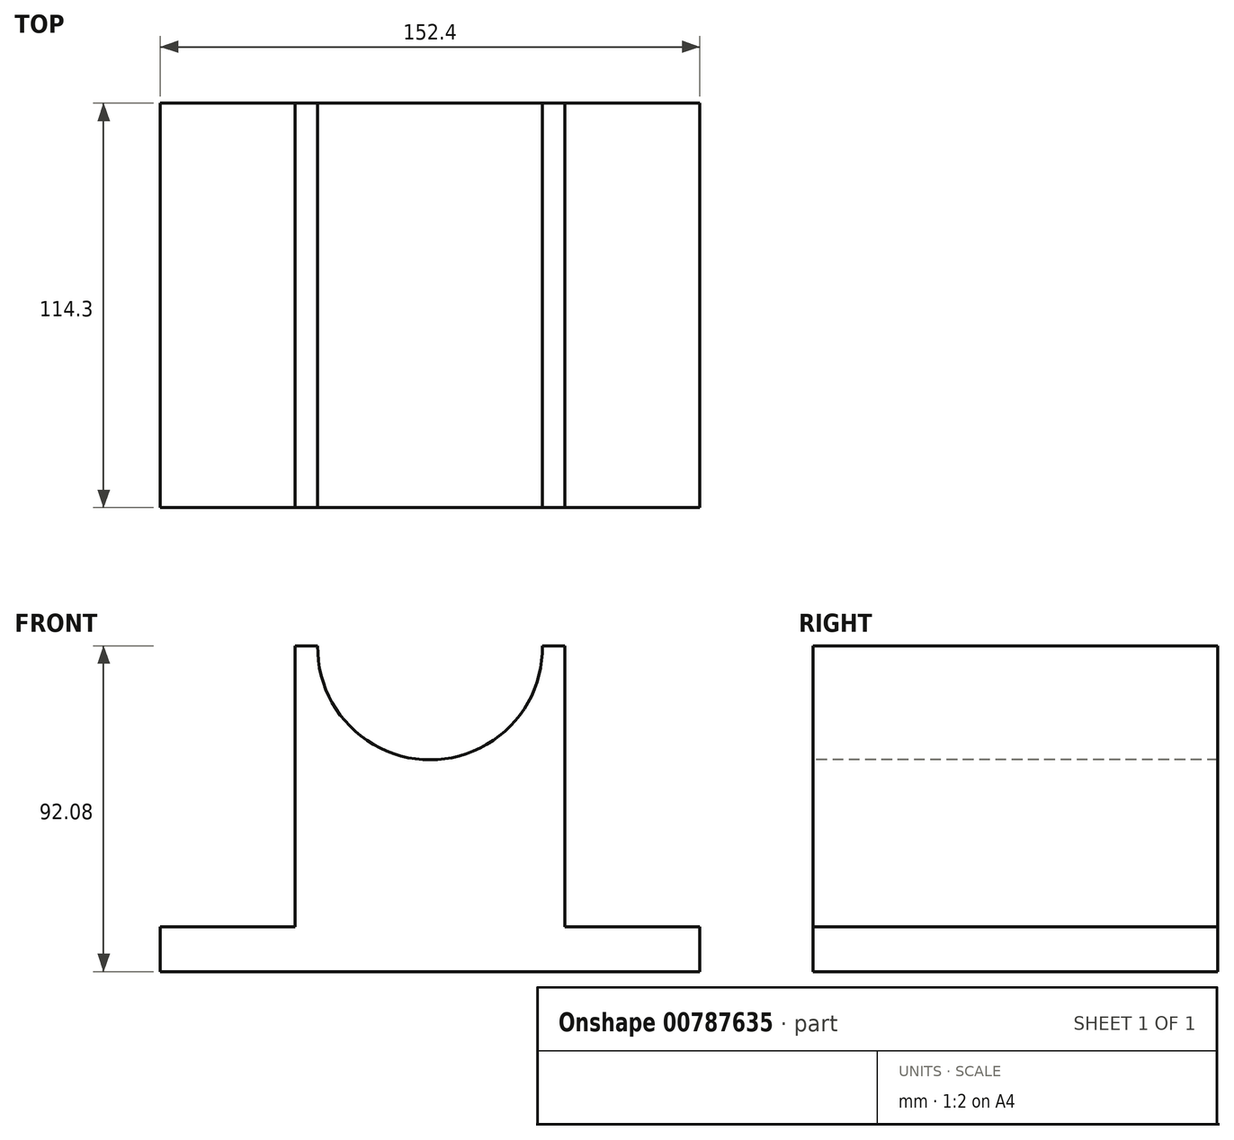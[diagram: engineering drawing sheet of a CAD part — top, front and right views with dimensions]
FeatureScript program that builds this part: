
annotation { "Feature Type Name" : "Feature", "Feature Type Description" : "" }
export const myFeature = defineFeature(function(context is Context, id is Id, definition is map)
    precondition{}
    {
        {
            var Q0;
            Q0=qCreatedBy(makeId("Front.planeOp"),FACE);
            var sketch = newSketch(context, id + "F0", { "sketchPlane" : qUnion([Q0])});
            skLineSegment(sketch, "E0", {"start": v(0, 0) * mm, "end": v(152.4, 0) * mm});
            skLineSegment(sketch, "E1", {"start": v(0, 0) * mm, "end": v(0, 92.08) * mm});
            skLineSegment(sketch, "E2", {"start": v(0, 92.08) * mm, "end": v(152.4, 92.08) * mm});
            skLineSegment(sketch, "E3", {"start": v(152.4, 92.08) * mm, "end": v(152.4, 0) * mm});
            skSolve(sketch);
        }
        {
            var Q0;
            Q0=makeQuery(id+"F0.imprint","IMPRINT",FACE,{"disambiguationData":[TD([[makeQuery(id+"F0.imprint","IMPRINT",EDGE,{"derivedFrom":sQuery(id+"F0.wireOp",EDGE,"E0")}),1.0]])]});
            extrude(context, id + "F1", {"entities" : qUnion([Q0]), "depth" : 114.3 * mm, "offsetDistance" : 25.4 * mm});
        }
        {
            var Q0;
            Q0=makeQuery(id+"F1.opExtrude","CAP_FACE",FACE,{"disambiguationData":[OSD([sQuery(id+"F0.wireOp",EDGE,"E0"),sQuery(id+"F0.wireOp",EDGE,"E1"),sQuery(id+"F0.wireOp",EDGE,"E2"),sQuery(id+"F0.wireOp",EDGE,"E3")])],"isStart":false});
            var sketch = newSketch(context, id + "F2", { "sketchPlane" : qUnion([Q0])});
            skLineSegment(sketch, "E4", {"start": v(152.4, 0) * mm, "end": v(152.4, 12.7) * mm});
            skLineSegment(sketch, "E5", {"start": v(152.4, 12.7) * mm, "end": v(114.3, 12.7) * mm});
            skLineSegment(sketch, "E6", {"start": v(0, 0) * mm, "end": v(0, 12.7) * mm});
            skLineSegment(sketch, "E7", {"start": v(0, 12.7) * mm, "end": v(38.1, 12.7) * mm});
            skLineSegment(sketch, "E8", {"start": v(38.1, 12.7) * mm, "end": v(38.1, 92.08) * mm});
            skLineSegment(sketch, "E9", {"start": v(114.3, 12.7) * mm, "end": v(114.3, 92.08) * mm});
            skSolve(sketch);
        }
        {
            var Q0;
            {var subQ0=sQuery(id+"F2.wireOp",EDGE,"E7");Q0=makeQuery(id+"F2.imprint","IMPRINT",FACE,{"disambiguationData":[TD([[makeQuery(id+"F2.imprint","IMPRINT",EDGE,{"derivedFrom":subQ0}),1.0]])]});}
            var Q1;
            {var subQ0=sQuery(id+"F2.wireOp",EDGE,"E5");Q1=makeQuery(id+"F2.imprint","IMPRINT",FACE,{"disambiguationData":[TD([[makeQuery(id+"F2.imprint","IMPRINT",EDGE,{"derivedFrom":subQ0}),-1.0]])]});}
            extrude(context, id + "F3", {"entities" : qUnion([Q0, Q1]), "operationType" : NewBodyOperationType.REMOVE, "endBound" : BoundingType.THROUGH_ALL, "oppositeDirection" : true, "depth" : 25.4 * mm, "offsetDistance" : 25.4 * mm});
        }
        {
            var Q0;
            Q0=makeQuery(id+"F1.opExtrude","CAP_FACE",FACE,{"disambiguationData":[OSD([sQuery(id+"F0.wireOp",EDGE,"E0"),sQuery(id+"F0.wireOp",EDGE,"E1"),sQuery(id+"F0.wireOp",EDGE,"E2"),sQuery(id+"F0.wireOp",EDGE,"E3")])],"isStart":false});
            var sketch = newSketch(context, id + "F4", { "sketchPlane" : qUnion([Q0])});
            skLineSegment(sketch, "E10", {"start": v(76.2, 92.08) * mm, "end": v(44.45, 92.08) * mm, "construction": true});
            skLineSegment(sketch, "E11", {"start": v(76.2, 92.08) * mm, "end": v(107.95, 92.08) * mm, "construction": true});
            skArc(sketch, "E12", {"start": v(44.45, 92.08) * mm, "mid": v(76.2, 59.85) * mm, "end": v(107.95, 92.07) * mm});
            skSolve(sketch);
        }
        {
            var Q0;
            {var subQ0=sQuery(id+"F4.wireOp",EDGE,"E12");Q0=makeQuery(id+"F4.imprint","IMPRINT",FACE,{"disambiguationData":[TD([[makeQuery(id+"F4.imprint","IMPRINT",EDGE,{"derivedFrom":subQ0}),1.0]])]});}
            extrude(context, id + "F5", {"entities" : qUnion([Q0]), "operationType" : NewBodyOperationType.REMOVE, "endBound" : BoundingType.THROUGH_ALL, "oppositeDirection" : true, "depth" : 25.4 * mm, "offsetDistance" : 25.4 * mm});
        }
    });
